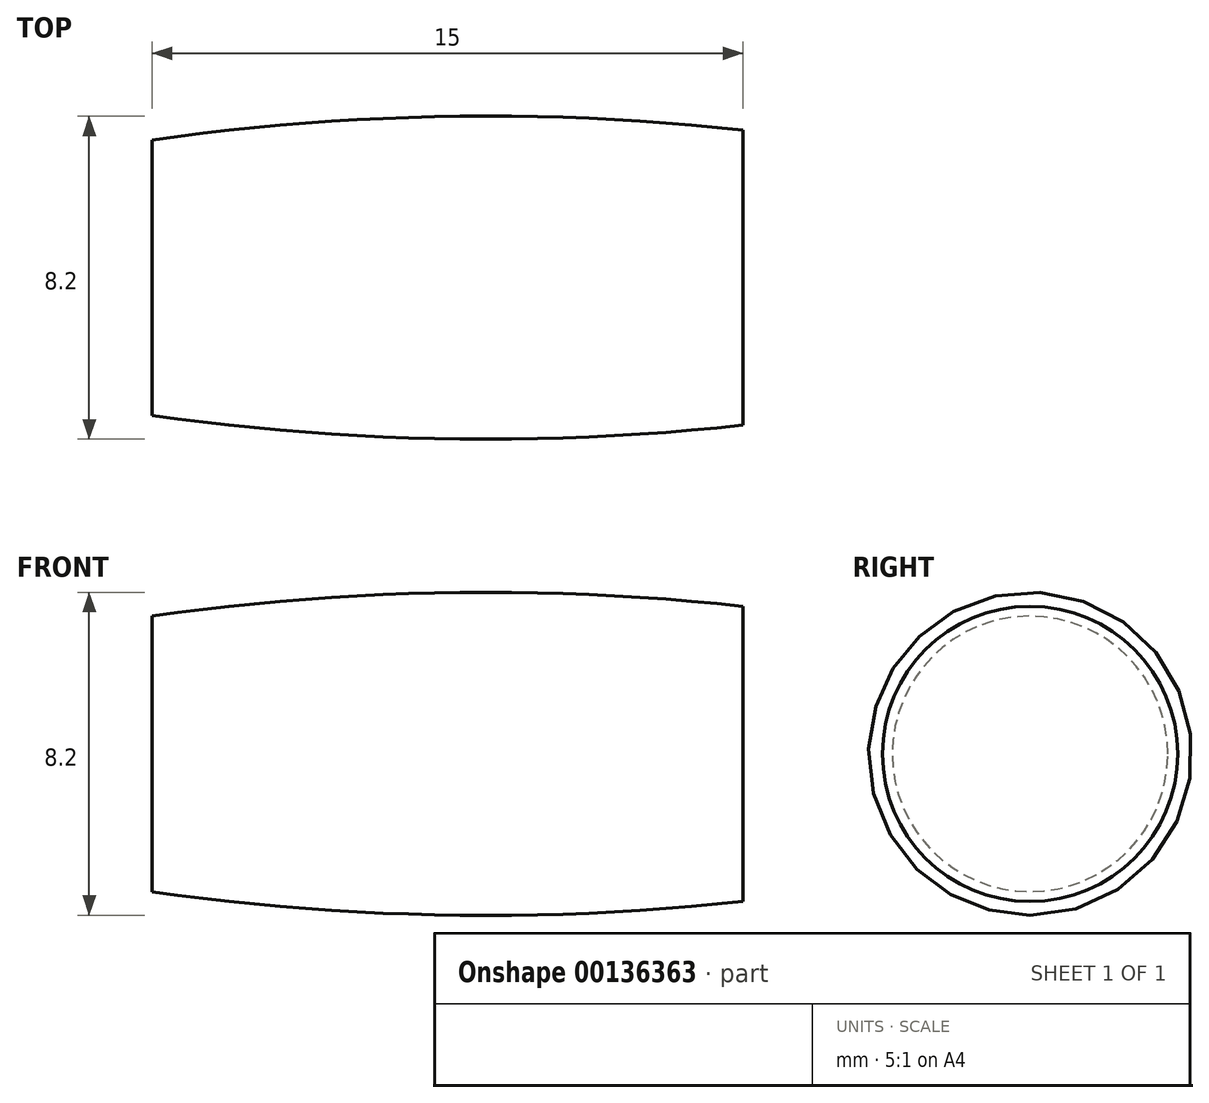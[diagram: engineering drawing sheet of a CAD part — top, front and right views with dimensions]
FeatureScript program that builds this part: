
annotation { "Feature Type Name" : "Feature", "Feature Type Description" : "" }
export const myFeature = defineFeature(function(context is Context, id is Id, definition is map)
    precondition{}
    {
        {
            var Q0;
            Q0=qCreatedBy(makeId("Right.planeOp"),FACE);
            cPlane(context, id + "F0", {"entities" : qUnion([Q0]), "cplaneType" : CPlaneType.OFFSET, "offset" : 15 * mm, "oppositeDirection" : true, "width" : 150 * mm, "height" : 150 * mm});
        }
        {
            var Q0;
            Q0=qCreatedBy(makeId("Right.planeOp"),FACE);
            var sketch = newSketch(context, id + "F1", { "sketchPlane" : qUnion([Q0])});
            skCircle(sketch, "E0", {"center": v(0, 0) * mm, "radius": 3.75 * mm});
            skSolve(sketch);
        }
        {
            var Q0;
            Q0=qCreatedBy(id+"F0.planeOp",FACE);
            var sketch = newSketch(context, id + "F2", { "sketchPlane" : qUnion([Q0])});
            skCircle(sketch, "E1", {"center": v(0, 0) * mm, "radius": 3.5 * mm});
            skSolve(sketch);
        }
        {
            var Q0;
            Q0=qCreatedBy(makeId("Front.planeOp"),FACE);
            var sketch = newSketch(context, id + "F3", { "sketchPlane" : qUnion([Q0])});
            skLineSegment(sketch, "E2", {"start": v(0, 0) * mm, "end": v(-15, 0) * mm, "construction": true});
            skArc(sketch, "E3", {"start": v(0, 3.75) * mm, "mid": v(-7.5, 4.1) * mm, "end": v(-15, 3.5) * mm});
            skArc(sketch, "E4.MirrorCS", {"start": v(0, -3.75) * mm, "mid": v(-7.5, -4.1) * mm, "end": v(-15, -3.5) * mm});
            skSolve(sketch);
        }
        {
            var Q0;
            Q0=makeQuery(id+"F2.imprint","IMPRINT",FACE,{"disambiguationData":[TD([[makeQuery(id+"F2.imprint","IMPRINT",EDGE,{"derivedFrom":sQuery(id+"F2.wireOp",EDGE,"E1")}),1.0]])]});
            var Q1;
            Q1=makeQuery(id+"F1.imprint","IMPRINT",FACE,{"disambiguationData":[TD([[makeQuery(id+"F1.imprint","IMPRINT",EDGE,{"derivedFrom":sQuery(id+"F1.wireOp",EDGE,"E0")}),1.0]])]});
            var Q2;
            Q2=sQuery(id+"F3.wireOp",EDGE,"E3");
            loft(context, id + "F4", {"addGuides" : true, "sheetProfilesArray" : [{ "sheetProfileEntities" : qUnion([Q0]) }, { "sheetProfileEntities" : qUnion([Q1]) }], "guidesArray" : [{ "guideEntities" : qUnion([Q2]), "guideDerivativeType" : LoftGuideDerivativeType.DEFAULT, "guideDerivativeMagnitude" : 1 }]});
        }
    });
